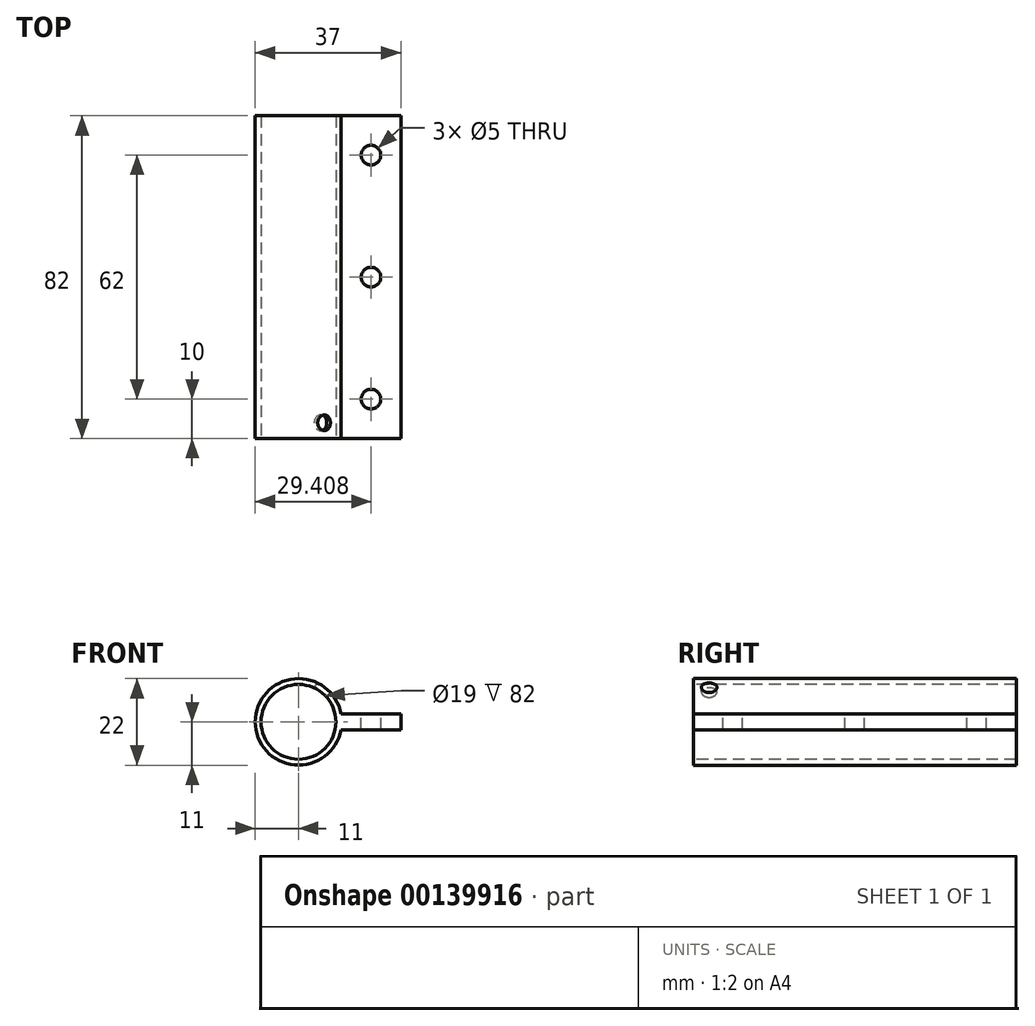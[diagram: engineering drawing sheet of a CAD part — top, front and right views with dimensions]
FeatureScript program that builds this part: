
annotation { "Feature Type Name" : "Feature", "Feature Type Description" : "" }
export const myFeature = defineFeature(function(context is Context, id is Id, definition is map)
    precondition{}
    {
        {
            var Q0;
            Q0=qCreatedBy(makeId("Front.planeOp"),FACE);
            var sketch = newSketch(context, id + "F0", { "sketchPlane" : qUnion([Q0])});
            skCircle(sketch, "E0", {"center": v(0, 0) * mm, "radius": 9.5 * mm});
            skCircle(sketch, "E1", {"center": v(0, 0) * mm, "radius": 11 * mm});
            skLineSegment(sketch, "E2", {"start": v(0, 0) * mm, "end": v(30, 0) * mm, "construction": true});
            skPoint(sketch, "E3", {"position": v(26, 0) * mm});
            skLineSegment(sketch, "E4", {"start": v(26, 2) * mm, "end": v(26, -2) * mm});
            skLineSegment(sketch, "E5", {"start": v(26, 2) * mm, "end": v(10.82, 2) * mm});
            skLineSegment(sketch, "E6", {"start": v(26, -2) * mm, "end": v(10.82, -2) * mm});
            skSolve(sketch);
        }
        {
            var Q0;
            Q0 = qSketchRegion(id + "F0", true);
            extrude(context, id + "F1", {"entities" : qUnion([Q0]), "oppositeDirection" : true, "depth" : 82 * mm});
        }
        {
            var Q0;
            Q0=makeQuery(id+"F1.opExtrude","SWEPT_FACE",FACE,{"disambiguationData":[OSD([sQuery(id+"F0.wireOp",EDGE,"E5")])]});
            var sketch = newSketch(context, id + "F2", { "sketchPlane" : qUnion([Q0])});
            skLineSegment(sketch, "E7.0", {"start": v(26, 82) * mm, "end": v(10.82, 82) * mm, "construction": true});
            skLineSegment(sketch, "E8.0", {"start": v(26, 0) * mm, "end": v(10.82, 0) * mm, "construction": true});
            skPoint(sketch, "E9", {"position": v(18.4, 82) * mm});
            skPoint(sketch, "E10", {"position": v(18.4, 0) * mm});
            skPoint(sketch, "E11", {"position": v(18.4, 41) * mm});
            skCircle(sketch, "E12", {"center": v(18.4, 41) * mm, "radius": 2.5 * mm});
            skPoint(sketch, "E13", {"position": v(18.4, 72) * mm});
            skPoint(sketch, "E14", {"position": v(18.4, 10) * mm});
            skCircle(sketch, "E15", {"center": v(18.4, 72) * mm, "radius": 2.5 * mm});
            skCircle(sketch, "E16", {"center": v(18.4, 10) * mm, "radius": 2.5 * mm});
            skSolve(sketch);
        }
        {
            var Q0;
            Q0=makeQuery(id+"F2.imprint","IMPRINT",FACE,{"disambiguationData":[TD([[makeQuery(id+"F2.imprint","IMPRINT",EDGE,{"derivedFrom":sQuery(id+"F2.wireOp",EDGE,"E15")}),1.0]])]});
            var Q1;
            Q1=makeQuery(id+"F2.imprint","IMPRINT",FACE,{"disambiguationData":[TD([[makeQuery(id+"F2.imprint","IMPRINT",EDGE,{"derivedFrom":sQuery(id+"F2.wireOp",EDGE,"E12")}),1.0]])]});
            var Q2;
            Q2=makeQuery(id+"F2.imprint","IMPRINT",FACE,{"disambiguationData":[TD([[makeQuery(id+"F2.imprint","IMPRINT",EDGE,{"derivedFrom":sQuery(id+"F2.wireOp",EDGE,"E16")}),1.0]])]});
            extrude(context, id + "F3", {"entities" : qUnion([Q0, Q1, Q2]), "operationType" : NewBodyOperationType.REMOVE, "oppositeDirection" : true, "depth" : 25 * mm});
        }
        {
            var Q0;
            Q0=makeQuery(id+"F1.opExtrude","CAP_FACE",FACE,{"disambiguationData":[OSD([sQuery(id+"F0.wireOp",EDGE,"E0"),sQuery(id+"F0.wireOp",EDGE,"E1"),sQuery(id+"F0.wireOp",EDGE,"E4"),sQuery(id+"F0.wireOp",EDGE,"E5"),sQuery(id+"F0.wireOp",EDGE,"E6")])],"isStart":true});
            var sketch = newSketch(context, id + "F4", { "sketchPlane" : qUnion([Q0])});
            skLineSegment(sketch, "E17.0", {"start": v(26, 2) * mm, "end": v(10.82, 2) * mm, "construction": true});
            skArc(sketch, "E18.0", {"start": v(10.82, 2) * mm, "mid": v(-11, 0) * mm, "end": v(10.82, -2) * mm, "construction": true});
            skCircle(sketch, "E19.0", {"center": v(0, 0) * mm, "radius": 9.5 * mm, "construction": true});
            skLineSegment(sketch, "E20", {"start": v(10.82, 2) * mm, "end": v(6.6, 8.8) * mm, "construction": true});
            skLineSegment(sketch, "E21", {"start": v(5.83, 9.38) * mm, "end": v(7.53, 8.1) * mm, "construction": true});
            skSolve(sketch);
        }
        {
            var Q0;
            Q0=sQuery(id+"F4.wireOp",EDGE,"E21");
            cPlane(context, id + "F5", {"entities" : qUnion([Q0]), "cplaneType" : CPlaneType.LINE_ANGLE, "offset" : 25 * mm, "angle" : 90 * degree, "width" : 150 * mm, "height" : 150 * mm});
        }
        {
            var Q0;
            Q0=qCreatedBy(id+"F5.planeOp",FACE);
            var sketch = newSketch(context, id + "F6", { "sketchPlane" : qUnion([Q0])});
            skLineSegment(sketch, "E22", {"start": v(0, 0) * mm, "end": v(0, 4) * mm, "construction": true});
            skCircle(sketch, "E23", {"center": v(0, 4) * mm, "radius": 2 * mm});
            skSolve(sketch);
        }
        {
            var Q0;
            Q0 = qSketchRegion(id + "F6", true);
            extrude(context, id + "F7", {"entities" : qUnion([Q0]), "operationType" : NewBodyOperationType.REMOVE, "oppositeDirection" : true, "depth" : 5 * mm});
        }
    });
